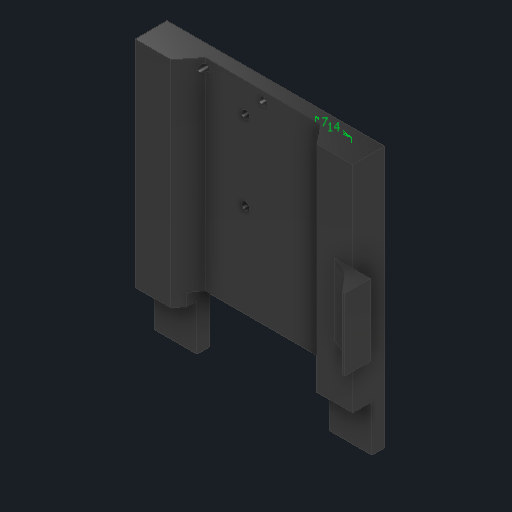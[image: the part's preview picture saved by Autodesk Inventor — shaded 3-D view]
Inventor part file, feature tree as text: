
AUTODESK INVENTOR PART (.ipt)
format: ipt  version: 2025 (Build 290162000, 162)  size: 290,304 bytes
history: native  units: mm
features: sketch x11, extrude x10, chamfer x4, other x3
ambient origin geometry x8: Origin, YZ Plane, XZ Plane, XY Plane, X Axis, Y Axis, Z Axis, Center Point
bodies: Solid1 (feature_tree)
feature tree (28):
  extrude  "Extrusion1"  Depth=102.0mm
  extrude  "Extrusion2"  Depth=1.6mm
  chamfer  "Chamfer1"  Distance=31.0mm
  chamfer  "Chamfer2"  Distance=31.0mm
  extrude  "Extrusion3"  Depth=7.0mm
  extrude  "Extrusion4"  Depth=7.0mm
  extrude  "Extrusion5"  Depth=7.0mm TaperAngle=0.0deg
  chamfer  "Chamfer3"  Distance=7.5mm
  chamfer  "Chamfer4"  Distance=7.5mm Angle=45.0deg
  extrude  "Extrusion6"  Depth=7.5mm TaperAngle=45.0deg
  extrude  "Extrusion7"  Depth=7.0mm TaperAngle=0.0deg
  extrude  "Extrusion8"  Depth=35.0mm
  extrude  "Extrusion10"  Depth=7.5mm
  extrude  "Extrusion11"  Depth=28.0mm
  sketch  "Sketch12"  dims[d12=3.2mm d13=31.0mm d14=31.0mm d15=3.2mm d16=3.2mm d17=50.0mm d18=0.0mm d19=7.5mm d20=0.0mm d21=6.0mm d22=7.5mm d23=45.0deg d24=6.0mm d25=7.5mm d26=45.0deg d27=69.75mm d28=0.0mm d29=35.0mm d30=7.5mm d31=28.0mm d32=7.0mm d33=3.0mm d34=0.0mm d35=7.0mm d36=10.0mm d37=0.0mm d38=7.0mm d39=3.0mm d40=45.0deg d41=6.0mm d42=7.0mm d43=45.0deg d44=30.0mm d45=10.0mm d46=21.0mm d47=13.0mm d48=10.0mm d49=0.0mm d50=36.0mm d51=0.0mm d52=12.0mm d53=0.0mm d57=6.0mm d58=14.0mm d59=0.0mm d60=45.0mm d61=0.0mm d62=7.0mm d63=14.0mm d55=0.5mm d56=0.872665mm]
  sketch  "Sketch1"  dims[d0=85.0mm d1=102.0mm]
  sketch  "Sketch2"  dims[d2=2.0mm d3=1.6mm]
  sketch  "Sketch3"  dims[d4=3.2mm]
  sketch  "Sketch4"  dims[d5=22.5mm]
  sketch  "Sketch5"  dims[d6=22.5mm]
  sketch  "Sketch6"  dims[d7=3.2mm]
  sketch  "Sketch7"  dims[d8=3.2mm]
  sketch  "Sketch8"  dims[d9=35.5mm]
  sketch  "Sketch10"  dims[d10=10.0mm]
  sketch  "Sketch11"  dims[d11=1.6mm]
  other  "Finish1"
  other  "Finish2"
  other  "Finish4"
